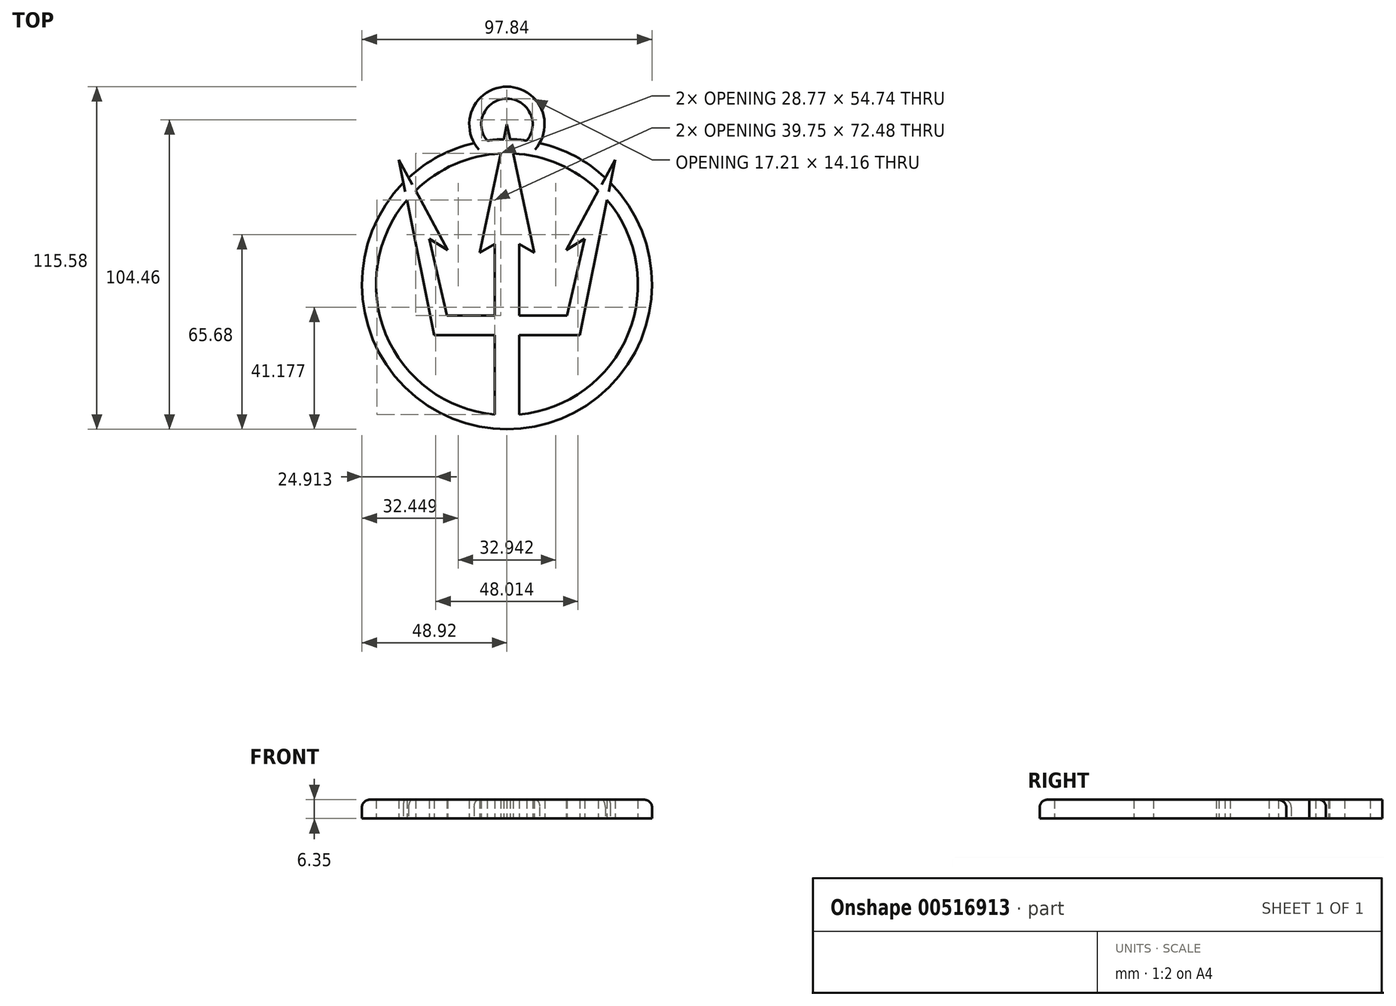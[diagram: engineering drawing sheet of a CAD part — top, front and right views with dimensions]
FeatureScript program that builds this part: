
annotation { "Feature Type Name" : "Feature", "Feature Type Description" : "" }
export const myFeature = defineFeature(function(context is Context, id is Id, definition is map)
    precondition{}
    {
        {
            var Q0;
            Q0=qCreatedBy(makeId("Top.planeOp"),FACE);
            var sketch = newSketch(context, id + "F0", { "sketchPlane" : qUnion([Q0])});
            skArc(sketch, "E0", {"start": v(33.2, 35.94) * mm, "mid": v(22.88, 43.24) * mm, "end": v(11.05, 47.66) * mm});
            skArc(sketch, "E1", {"start": v(30.86, 31.62) * mm, "mid": v(17.62, 40.51) * mm, "end": v(2.09, 44.13) * mm});
            skLineSegment(sketch, "E2", {"start": v(4.13, 0) * mm, "end": v(4.13, -10.6) * mm});
            skLineSegment(sketch, "E3", {"start": v(4.13, -10.6) * mm, "end": v(20.3, -10.6) * mm});
            skLineSegment(sketch, "E4", {"start": v(20.3, -10.6) * mm, "end": v(26.26, 15.32) * mm});
            skLineSegment(sketch, "E5", {"start": v(26.26, 15.32) * mm, "end": v(20.02, 11.54) * mm});
            skLineSegment(sketch, "E6", {"start": v(20.02, 11.54) * mm, "end": v(30.86, 31.62) * mm});
            skLineSegment(sketch, "E7", {"start": v(4.13, 0) * mm, "end": v(4.13, 13.53) * mm});
            skLineSegment(sketch, "E8", {"start": v(4.13, 13.53) * mm, "end": v(9.18, 10.72) * mm});
            skLineSegment(sketch, "E9", {"start": v(9.18, 10.72) * mm, "end": v(2.09, 44.13) * mm});
            skLineSegment(sketch, "E10", {"start": v(4.13, -17.2) * mm, "end": v(24.56, -17.2) * mm});
            skLineSegment(sketch, "E11", {"start": v(24.56, -17.2) * mm, "end": v(33.76, 28.5) * mm});
            skLineSegment(sketch, "E12.trimOffspring", {"start": v(33.2, 35.94) * mm, "end": v(36.49, 42.05) * mm});
            skLineSegment(sketch, "E13.trimOffspring", {"start": v(34.92, 34.27) * mm, "end": v(36.49, 42.05) * mm});
            skLineSegment(sketch, "E14.trimOffspring", {"start": v(1.07, 48.91) * mm, "end": v(0, 53.95) * mm});
            skLineSegment(sketch, "E15", {"start": v(4.13, -17.2) * mm, "end": v(4.13, -43.98) * mm});
            skLineSegment(sketch, "E16.MirrorCS", {"start": v(-1.07, 48.91) * mm, "end": v(0, 53.95) * mm});
            skLineSegment(sketch, "E17.MirrorCS", {"start": v(-4.13, 0) * mm, "end": v(-4.13, 13.53) * mm});
            skLineSegment(sketch, "E18.MirrorCS", {"start": v(-4.13, 0) * mm, "end": v(-4.13, -10.6) * mm});
            skLineSegment(sketch, "E19.MirrorCS", {"start": v(-9.18, 10.72) * mm, "end": v(-2.09, 44.13) * mm});
            skLineSegment(sketch, "E20.MirrorCS", {"start": v(-4.13, 13.53) * mm, "end": v(-9.18, 10.72) * mm});
            skLineSegment(sketch, "E21.MirrorCS", {"start": v(-4.13, -10.6) * mm, "end": v(-20.3, -10.6) * mm});
            skLineSegment(sketch, "E22.MirrorCS", {"start": v(-4.13, -17.2) * mm, "end": v(-24.56, -17.2) * mm});
            skLineSegment(sketch, "E23.MirrorCS", {"start": v(-24.56, -17.2) * mm, "end": v(-33.76, 28.5) * mm});
            skLineSegment(sketch, "E24.MirrorCS", {"start": v(-20.02, 11.54) * mm, "end": v(-30.86, 31.62) * mm});
            skLineSegment(sketch, "E25.MirrorCS", {"start": v(-26.26, 15.32) * mm, "end": v(-20.02, 11.54) * mm});
            skLineSegment(sketch, "E26.MirrorCS", {"start": v(-20.3, -10.6) * mm, "end": v(-26.26, 15.32) * mm});
            skLineSegment(sketch, "E27.MirrorCS", {"start": v(-33.2, 35.94) * mm, "end": v(-36.49, 42.05) * mm});
            skLineSegment(sketch, "E28.MirrorCS", {"start": v(-34.92, 34.27) * mm, "end": v(-36.49, 42.05) * mm});
            skLineSegment(sketch, "E29.MirrorCS", {"start": v(-4.13, -17.2) * mm, "end": v(-4.13, -43.98) * mm});
            skArc(sketch, "E30.trimOffspring", {"start": v(-33.76, 28.5) * mm, "mid": v(-40.9, -16.71) * mm, "end": v(-4.13, -43.98) * mm});
            skArc(sketch, "E31.trimOffspring", {"start": v(-34.92, 34.27) * mm, "mid": v(0, -48.92) * mm, "end": v(34.92, 34.27) * mm});
            skArc(sketch, "E32.trimOffspring", {"start": v(-2.09, 44.13) * mm, "mid": v(-17.62, 40.51) * mm, "end": v(-30.86, 31.62) * mm});
            skArc(sketch, "E33.trimOffspring", {"start": v(-1.07, 48.91) * mm, "mid": v(-3.9, 48.77) * mm, "end": v(-6.71, 48.46) * mm});
            skArc(sketch, "E34.trimOffspring", {"start": v(4.13, -43.98) * mm, "mid": v(40.9, -16.71) * mm, "end": v(33.76, 28.5) * mm});
            skArc(sketch, "E35", {"start": v(11.05, 47.66) * mm, "mid": v(0, 66.66) * mm, "end": v(-11.05, 47.66) * mm});
            skArc(sketch, "E36", {"start": v(6.71, 48.46) * mm, "mid": v(0, 62.62) * mm, "end": v(-6.71, 48.46) * mm});
            skArc(sketch, "E37.trimOffspring", {"start": v(-11.05, 47.66) * mm, "mid": v(-22.88, 43.24) * mm, "end": v(-33.2, 35.94) * mm});
            skArc(sketch, "E38.trimOffspring", {"start": v(6.71, 48.46) * mm, "mid": v(3.9, 48.77) * mm, "end": v(1.07, 48.91) * mm});
            skSolve(sketch);
        }
        {
            var Q0;
            Q0=makeQuery(id+"F0.imprint","IMPRINT",FACE,{"disambiguationData":[TD([[makeQuery(id+"F0.imprint","IMPRINT",EDGE,{"derivedFrom":sQuery(id+"F0.wireOp",EDGE,"E0")}),1.0]])]});
            extrude(context, id + "F1", {"entities" : qUnion([Q0]), "depth" : 6.35 * mm, "offsetDistance" : 25.4 * mm});
        }
        {
            var Q0;
            Q0=makeQuery(id+"F1.opExtrude","CAP_EDGE",EDGE,{"disambiguationData":[OSD([sQuery(id+"F0.wireOp",EDGE,"E37.trimOffspring")])],"isStart":false});
            fillet(context, id + "F2", {"entities" : qUnion([Q0]), "radius" : 2.54 * mm, "tangentPropagation" : true, "allowEdgeOverflow" : false});
        }
        {
            var Q0;
            Q0=makeQuery(id+"F1.opExtrude","CAP_EDGE",EDGE,{"disambiguationData":[OSD([sQuery(id+"F0.wireOp",EDGE,"E31.trimOffspring")])],"isStart":false});
            fillet(context, id + "F3", {"entities" : qUnion([Q0]), "radius" : 2.54 * mm, "tangentPropagation" : true, "allowEdgeOverflow" : false});
        }
        {
            var Q0;
            Q0=makeQuery(id+"F1.opExtrude","CAP_EDGE",EDGE,{"disambiguationData":[OSD([sQuery(id+"F0.wireOp",EDGE,"E0")])],"isStart":false});
            fillet(context, id + "F4", {"entities" : qUnion([Q0]), "radius" : 2.54 * mm, "tangentPropagation" : true, "allowEdgeOverflow" : false});
        }
    });
